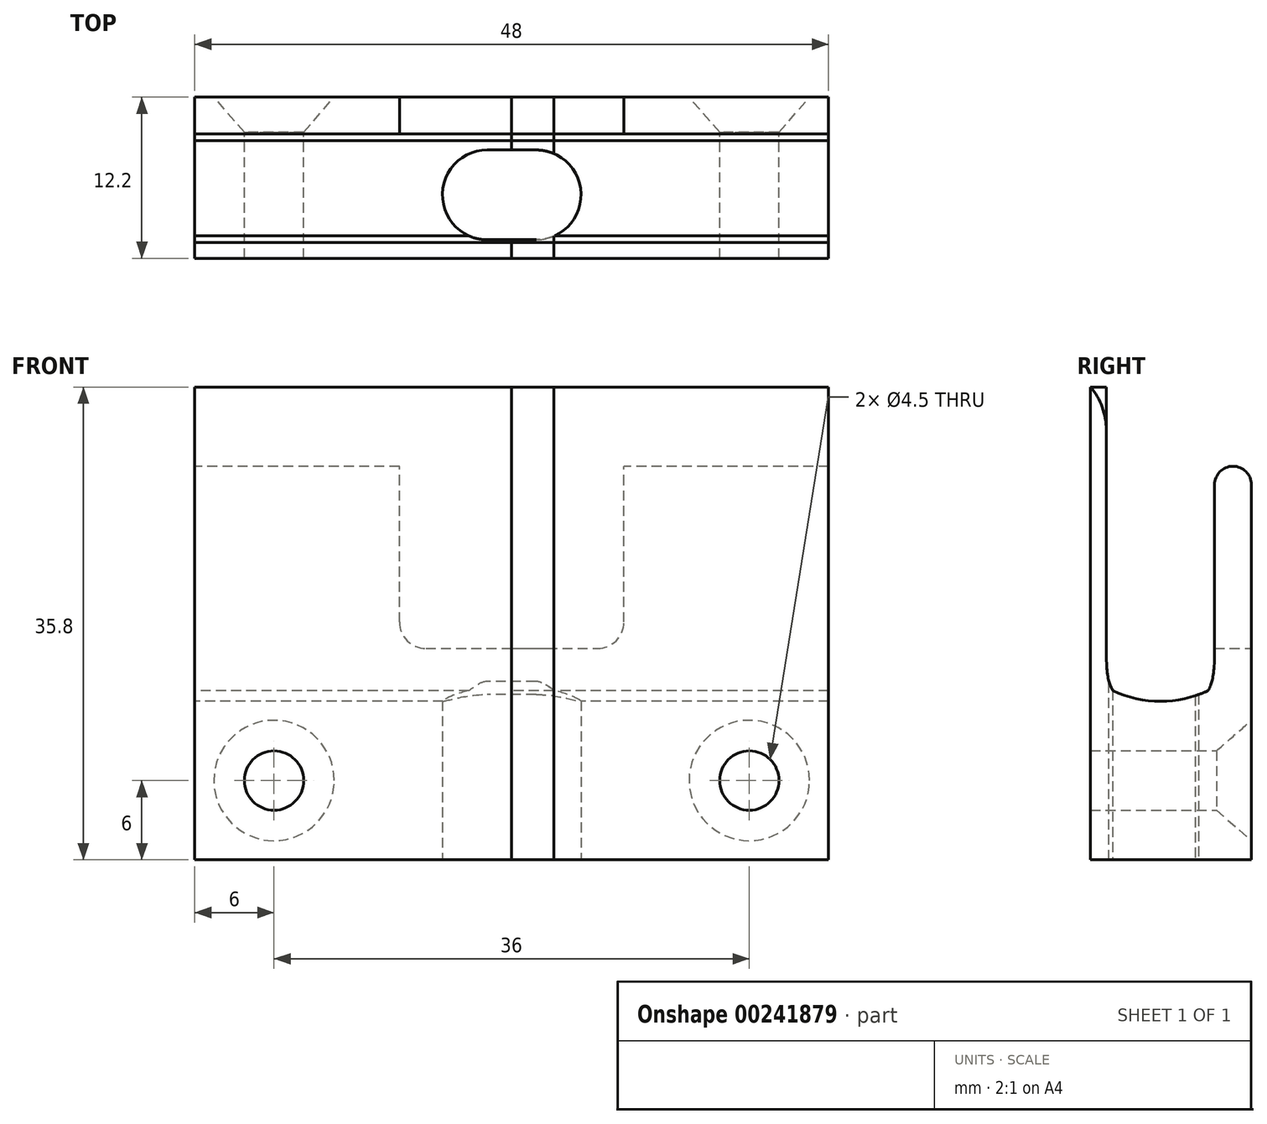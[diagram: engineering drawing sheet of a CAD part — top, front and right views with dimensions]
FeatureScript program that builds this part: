
annotation { "Feature Type Name" : "Feature", "Feature Type Description" : "" }
export const myFeature = defineFeature(function(context is Context, id is Id, definition is map)
    precondition{}
    {
        {
            var Q0;
            Q0=qCreatedBy(makeId("Right.planeOp"),FACE);
            var sketch = newSketch(context, id + "F0", { "sketchPlane" : qUnion([Q0])});
            skLineSegment(sketch, "E0", {"start": v(1.2, 35.8) * mm, "end": v(1.2, 15.8) * mm});
            skLineSegment(sketch, "E1", {"start": v(9.4, 29.8) * mm, "end": v(9.4, 15.8) * mm});
            skLineSegment(sketch, "E2", {"start": v(1.2, 35.8) * mm, "end": v(0, 35.8) * mm});
            skLineSegment(sketch, "E3", {"start": v(0, 35.8) * mm, "end": v(0, 0) * mm});
            skLineSegment(sketch, "E4", {"start": v(0, 0) * mm, "end": v(12.2, 0) * mm});
            skLineSegment(sketch, "E5", {"start": v(12.2, 0) * mm, "end": v(12.2, 29.8) * mm});
            skLineSegment(sketch, "E6", {"start": v(12.2, 29.8) * mm, "end": v(9.4, 29.8) * mm});
            skPoint(sketch, "E7", {"position": v(12.2, 22.8) * mm});
            skFitSpline(sketch, "E8", {"points": [v(1.2, 15.8) * mm, v(1.7, 12.8) * mm], "startDerivative": vector(0, -6.11) * mm, "endDerivative": vector(0.75, -1.24) * mm});
            skArc(sketch, "E9", {"start": v(1.7, 12.8) * mm, "mid": v(5.3, 12) * mm, "end": v(8.9, 12.8) * mm});
            skLineSegment(sketch, "E10", {"start": v(5.3, 15.8) * mm, "end": v(5.3, 13.98) * mm, "construction": true});
            skLineSegment(sketch, "E11", {"start": v(1.2, 15.8) * mm, "end": v(9.4, 15.8) * mm, "construction": true});
            skFitSpline(sketch, "E12.MirrorCS", {"points": [v(9.4, 15.8) * mm, v(8.9, 12.8) * mm], "startDerivative": vector(0, -6.11) * mm, "endDerivative": vector(-0.75, -1.24) * mm});
            skLineSegment(sketch, "E13", {"start": v(1.7, 12.8) * mm, "end": v(8.9, 12.8) * mm, "construction": true});
            skSolve(sketch);
        }
        {
            var Q0;
            Q0=makeQuery(id+"F0.imprint","IMPRINT",FACE,{"disambiguationData":[TD([[makeQuery(id+"F0.imprint","IMPRINT",EDGE,{"derivedFrom":sQuery(id+"F0.wireOp",EDGE,"E0")}),-1.0]])]});
            extrude(context, id + "F1", {"entities" : qUnion([Q0]), "depth" : 3.2 * mm});
        }
        {
            var Q0;
            Q0=makeQuery(id+"F0.imprint","IMPRINT",FACE,{"disambiguationData":[TD([[makeQuery(id+"F0.imprint","IMPRINT",EDGE,{"derivedFrom":sQuery(id+"F0.wireOp",EDGE,"E0")}),-1.0]])]});
            extrude(context, id + "F2", {"entities" : qUnion([Q0]), "endBound" : BoundingType.SYMMETRIC, "depth" : 48 * mm});
        }
        {
            var Q0;
            Q0=qCreatedBy(makeId("Top.planeOp"),FACE);
            var sketch = newSketch(context, id + "F3", { "sketchPlane" : qUnion([Q0])});
            skLineSegment(sketch, "E14", {"start": v(-1.85, 4.8) * mm, "end": v(1.85, 4.8) * mm, "construction": true});
            skLineSegment(sketch, "E15", {"start": v(-1.85, 8.2) * mm, "end": v(1.85, 8.2) * mm});
            skLineSegment(sketch, "E16", {"start": v(-1.85, 1.4) * mm, "end": v(1.85, 1.4) * mm});
            skArc(sketch, "E17", {"start": v(-1.85, 8.2) * mm, "mid": v(-5.25, 4.8) * mm, "end": v(-1.85, 1.4) * mm});
            skArc(sketch, "E18", {"start": v(1.85, 1.4) * mm, "mid": v(5.25, 4.8) * mm, "end": v(1.85, 8.2) * mm});
            skPoint(sketch, "E19", {"position": v(0, 4.8) * mm});
            skSolve(sketch);
        }
        {
            var Q0;
            Q0=makeQuery(id+"F3.imprint","IMPRINT",FACE,{"disambiguationData":[TD([[makeQuery(id+"F3.imprint","IMPRINT",EDGE,{"derivedFrom":sQuery(id+"F3.wireOp",EDGE,"E15")}),-1.0]])]});
            extrude(context, id + "F4", {"entities" : qUnion([Q0]), "operationType" : NewBodyOperationType.REMOVE, "endBound" : BoundingType.THROUGH_ALL, "depth" : 25 * mm});
        }
        {
            var Q0;
            Q0=makeQuery(id+"F2.opExtrude","SWEPT_FACE",FACE,{"disambiguationData":[OSD([sQuery(id+"F0.wireOp",EDGE,"E5")])]});
            var sketch = newSketch(context, id + "F5", { "sketchPlane" : qUnion([Q0])});
            skPoint(sketch, "E20", {"position": v(-18, 6) * mm});
            skPoint(sketch, "E21", {"position": v(18, 6) * mm});
            skLineSegment(sketch, "E22", {"start": v(-18, 6) * mm, "end": v(18, 6) * mm, "construction": true});
            skPoint(sketch, "E23", {"position": v(0, 6) * mm});
            skLineSegment(sketch, "E24.bottom", {"start": v(8.5, 16) * mm, "end": v(-8.5, 16) * mm});
            skLineSegment(sketch, "E24.top", {"start": v(8.5, 30.77) * mm, "end": v(-8.5, 30.77) * mm});
            skLineSegment(sketch, "E24.left", {"start": v(8.5, 16) * mm, "end": v(8.5, 30.77) * mm});
            skLineSegment(sketch, "E24.right", {"start": v(-8.5, 16) * mm, "end": v(-8.5, 30.77) * mm});
            skPoint(sketch, "E24.middle", {"position": v(0, 23.38) * mm});
            skSolve(sketch);
        }
        {
            var Q0;
            {var subQ0=sQuery(id+"F5.wireOp",EDGE,"E24.bottom");Q0=makeQuery(id+"F5.imprint","IMPRINT",FACE,{"disambiguationData":[TD([[makeQuery(id+"F5.imprint","IMPRINT",EDGE,{"derivedFrom":subQ0}),-1.0]])]});}
            var Q1;
            Q1=makeQuery(id+"F2.opExtrude","SWEPT_FACE",FACE,{"disambiguationData":[OSD([sQuery(id+"F0.wireOp",EDGE,"E1")])]});
            extrude(context, id + "F6", {"entities" : qUnion([Q0]), "operationType" : NewBodyOperationType.REMOVE, "endBound" : BoundingType.UP_TO_SURFACE, "oppositeDirection" : true, "endBoundEntityFace" : qUnion([Q1]), "depth" : 25 * mm});
        }
        {
            var Q0;
            Q0=makeQuery(id+"F2.opExtrude","SWEPT_EDGE",EDGE,{"disambiguationData":[OSD([sQuery(id+"F0.wireOp",EDGE,"E5"),sQuery(id+"F0.wireOp",EDGE,"E6")])]});
            var Q1;
            Q1=makeQuery(id+"F2.opExtrude","SWEPT_EDGE",EDGE,{"disambiguationData":[OSD([sQuery(id+"F0.wireOp",EDGE,"E1"),sQuery(id+"F0.wireOp",EDGE,"E6")])]});
            fillet(context, id + "F7", {"entities" : qUnion([Q0, Q1]), "radius" : 1.4 * mm, "tangentPropagation" : true, "allowEdgeOverflow" : false});
        }
        {
            var Q0;
            Q0=makeQuery(id+"F2.opExtrude","SWEPT_EDGE",EDGE,{"disambiguationData":[OSD([sQuery(id+"F0.wireOp",EDGE,"E0"),sQuery(id+"F0.wireOp",EDGE,"E2")])]});
            fillet(context, id + "F8", {"entities" : qUnion([Q0]), "radius" : 5 * mm, "tangentPropagation" : true, "allowEdgeOverflow" : false});
        }
        {
            var Q0;
            Q0=makeQuery(id+"F6.boolean.opBoolean","COPY",EDGE,{"derivedFrom":makeQuery(id+"F6.opExtrude","SWEPT_EDGE",EDGE,{"disambiguationData":[OSD([sQuery(id+"F5.wireOp",EDGE,"E24.bottom"),sQuery(id+"F5.wireOp",EDGE,"E24.right")])]})});
            var Q1;
            Q1=makeQuery(id+"F6.boolean.opBoolean","COPY",EDGE,{"derivedFrom":makeQuery(id+"F6.opExtrude","SWEPT_EDGE",EDGE,{"disambiguationData":[OSD([sQuery(id+"F5.wireOp",EDGE,"E24.bottom"),sQuery(id+"F5.wireOp",EDGE,"E24.left")])]})});
            fillet(context, id + "F9", {"entities" : qUnion([Q0, Q1]), "radius" : 2 * mm, "tangentPropagation" : true, "allowEdgeOverflow" : false});
        }
        {
            var Q0;
            Q0=sQuery(id+"F5.wireOp",VERTEX,"E20");
            var Q1;
            Q1=sQuery(id+"F5.wireOp",VERTEX,"E21");
            var Q2;
            Q2=makeQuery(id+"F2.opExtrude","SWEPT_BODY",BODY,{"disambiguationData":[OSD([sQuery(id+"F0.wireOp",EDGE,"E0"),sQuery(id+"F0.wireOp",EDGE,"E1"),sQuery(id+"F0.wireOp",EDGE,"b5ba47e6-b76f-4501-b9c3-fb76180505b7"),sQuery(id+"F0.wireOp",EDGE,"a10aeb3f-0070-47ff-a5a4-3e3e14a23485"),sQuery(id+"F0.wireOp",EDGE,"E2"),sQuery(id+"F0.wireOp",EDGE,"E3"),sQuery(id+"F0.wireOp",EDGE,"E4"),sQuery(id+"F0.wireOp",EDGE,"E5"),sQuery(id+"F0.wireOp",EDGE,"E6")])]});
            hole(context, id + "F10", {"style" : HoleStyle.C_SINK, "endStyle" : HoleEndStyle.THROUGH, "standardTappedOrClearance" : lookupTablePath({ "standard" : "ANSI", "fit" : "Normal (ASME)", "size" : "#8", "type" : "Clearance" }), "standardBlindInLast" : lookupTablePath({ "fit" : "Free", "standard" : "ANSI", "size" : "#8", "type" : "Clearance" }), "holeDiameter" : 4.5 * mm, "cSinkDiameter" : 9.12 * mm, "cSinkAngle" : 82 * degree, "locations" : qUnion([Q0, Q1]), "scope" : qUnion([Q2]), "isTappedThrough" : true});
        }
    });
